# Revit family: TechoLED MOON SERIES
name_source: partatom
category: Lighting Fixtures
units: mm (PartAtom-declared; Revit-internal decimal feet)

## family parameters
Always vertical = Yes
Cut with Voids When Loaded = No
Host = Ceiling
Light Source = Yes
Part Type = Normal
Room Calculation Point = No
Round Connector Dimension = Use Diameter
Shared = No

## types (1)
- TechoLED-MS-DI-35-120W
    Apparent Load = 150 VA
    Color Filter = 16777215
    Default Elevation = 0' - 0"
    Description = 35" Indoor LED Fixture Pendant Mounted
    Dimming Lamp Color Temperature Shift = <None>
    Distribution = Direct/Indirect
    Driver Options = 0 - 10V Dimming
    FINISH - REFLECTOR = Dynamic White
    FIXTURE ID = MS - Circle
    MOUNTING = Pendant
    Manufacturer = TechoLED
    Model = TechoLED-MS-DI-35-120W
    Photometric Web File = TECHOLED-MS-DI-35-120.ies
    Tilt Angle = 90.00°
    Type Comments = MOON SERIES
    URL = https://techoled.com
    Voltage = 277 V
    Wattage Comments = 120W

## geometry (parser evidence)
native form markers: Sweep x1
no freeform markers — native parametric forms only
